# Revit family: 1382xxx Zero Square (UL)
name_source: partatom
category: Lighting Fixtures
revit_build: Autodesk Revit 2018 (Build: 20170223_1515(x64)
units: mm (PartAtom-declared; Revit-internal decimal feet)

## family parameters
Always vertical = Yes
Cut with Voids When Loaded = No
Host = Ceiling
Light Source = Yes
OmniClass Number = 23.80.70.11
OmniClass Title = Luminaries for Internal Lighting
Part Type = Normal
Room Calculation Point = No
Round Connector Dimension = Use Diameter
Shared = No

## types (1)
- Astro Zero Square
    ADA compliant = Yes
    Color Filter = 16777215
    Dimmable = Yes
    Dimming Lamp Color Temperature Shift = <None>
    Dimming Method = 0-10V
    Driver Included = Yes
    Driver Required = No
    Efficacy (lm/w) = 62
    Electrical Class = 1
    Lamp = LED
    Light Source Fixed = Yes
    Location / IP Rating = Dry
    Main Finish = Matt White
    Main Material = Metal - Mild Steel
    Manufacturer URL - Europe and Rest of World = www.astrolighting.com
    Manufacturer URL - North America = us.astrolighting.com
    Photometric Web File = 1382003_Zero Square_Photometry_IES_Iss. 01.ies
    Power (Watts) = 16.8
    Product CCT = 3000K
    Product CRI = 90
    Product Dimensions (MM) = 400x400x50
    Product Location = Interior
    Product Name = Zero Square
    Product SKU = 1382003
    Product URL = https://us.astrolighting.com
    Product Weight (KG) = 3 mm  [stored 0.00984252 ft]
    Tilt Angle = 90.00°

note: [stored X ft] marks values corroborated as IEEE doubles in the binary element streams (Revit-internal decimal feet)

## geometry (parser evidence)
native form markers: Sweep x1
no freeform markers — native parametric forms only
